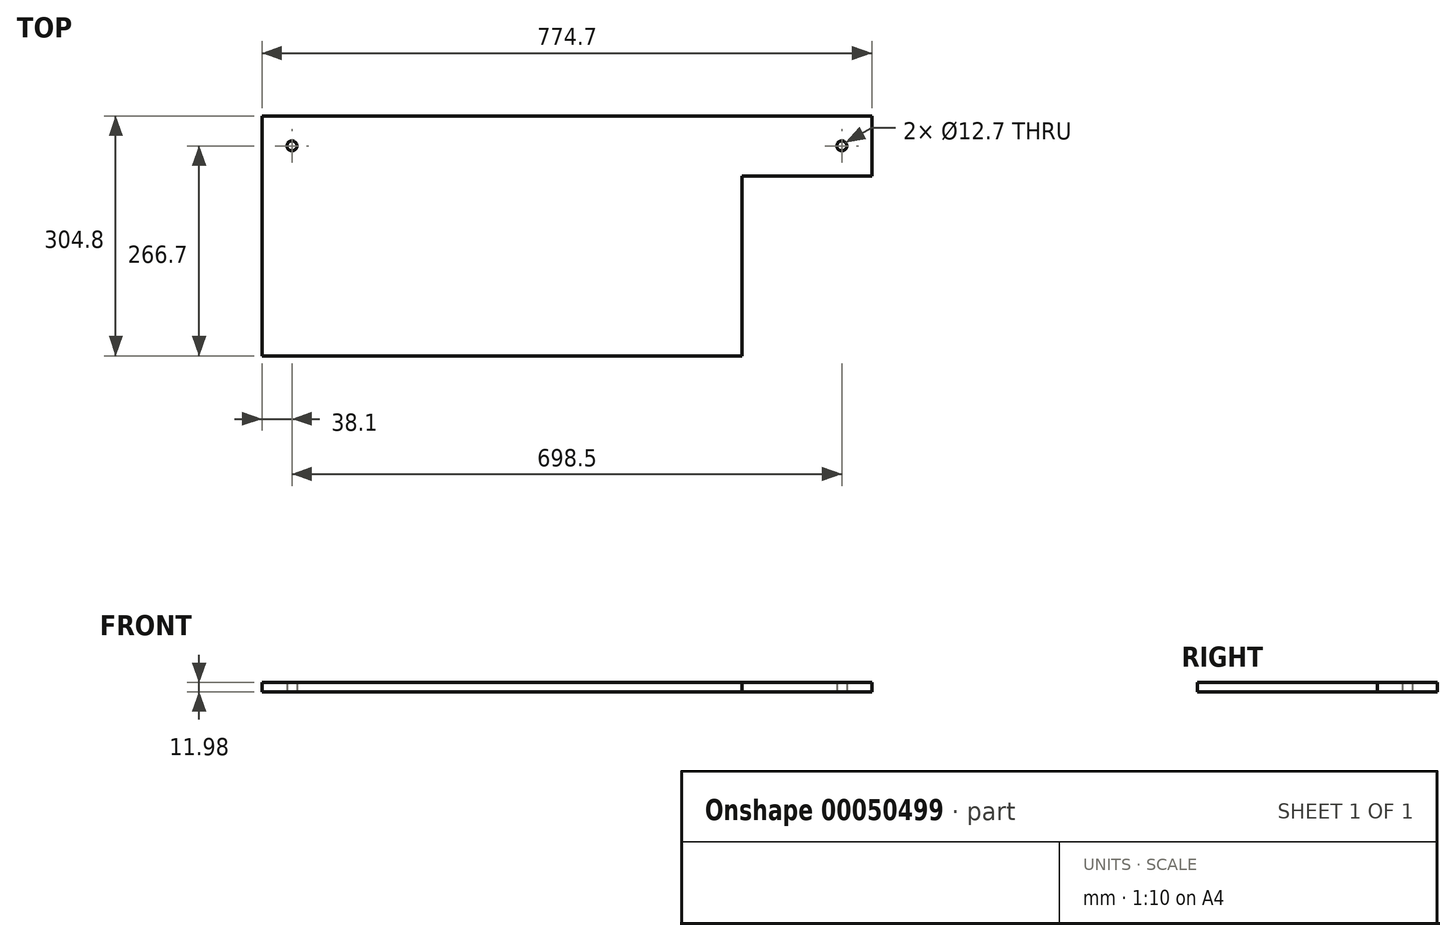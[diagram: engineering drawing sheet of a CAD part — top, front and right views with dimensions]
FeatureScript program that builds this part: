
annotation { "Feature Type Name" : "Feature", "Feature Type Description" : "" }
export const myFeature = defineFeature(function(context is Context, id is Id, definition is map)
    precondition{}
    {
        {
            var Q0;
            Q0=qCreatedBy(makeId("Top.planeOp"),FACE);
            var sketch = newSketch(context, id + "F0", { "sketchPlane" : qUnion([Q0])});
            skLineSegment(sketch, "E0.rect.bottom", {"start": v(387.35, 38.1) * mm, "end": v(-387.35, 38.1) * mm});
            skLineSegment(sketch, "E0.rect.top", {"start": v(387.35, -38.1) * mm, "end": v(222.25, -38.1) * mm});
            skLineSegment(sketch, "E0.rect.left", {"start": v(387.35, 38.1) * mm, "end": v(387.35, -38.1) * mm});
            skLineSegment(sketch, "E0.rect.right", {"start": v(-387.35, 38.1) * mm, "end": v(-387.35, -38.1) * mm});
            skPoint(sketch, "E0.rect.middle", {"position": v(0, 0) * mm});
            skLineSegment(sketch, "E1", {"start": v(222.25, -38.1) * mm, "end": v(222.25, -266.7) * mm});
            skLineSegment(sketch, "E2", {"start": v(222.25, -266.7) * mm, "end": v(-387.35, -266.7) * mm});
            skLineSegment(sketch, "E3", {"start": v(-387.35, -266.7) * mm, "end": v(-387.35, -38.1) * mm});
            skSolve(sketch);
        }
        {
            var Q0;
            Q0=qSketchRegion(id+"F0",true);
            extrude(context, id + "F1", {"entities" : qUnion([Q0]), "endBound" : BoundingType.SYMMETRIC, "depth" : 12 * mm});
        }
        {
            var Q0;
            Q0=makeQuery(id+"F1.opExtrude","CAP_FACE",FACE,{"disambiguationData":[OSD([sQuery(id+"F0.wireOp",EDGE,"E0.rect.bottom"),sQuery(id+"F0.wireOp",EDGE,"E0.rect.top"),sQuery(id+"F0.wireOp",EDGE,"E0.rect.left"),sQuery(id+"F0.wireOp",EDGE,"E0.rect.right"),sQuery(id+"F0.wireOp",EDGE,"E1"),sQuery(id+"F0.wireOp",EDGE,"E2"),sQuery(id+"F0.wireOp",EDGE,"E3")])],"isStart":true});
            var sketch = newSketch(context, id + "F2", { "sketchPlane" : qUnion([Q0])});
            skCircle(sketch, "E4", {"center": v(-349.25, 0) * mm, "radius": 6.35 * mm});
            skCircle(sketch, "E5", {"center": v(349.25, 0) * mm, "radius": 6.35 * mm});
            skSolve(sketch);
        }
        {
            var Q0;
            Q0 = qSketchRegion(id + "F2", true);
            extrude(context, id + "F3", {"entities" : qUnion([Q0]), "operationType" : NewBodyOperationType.REMOVE, "endBound" : BoundingType.UP_TO_NEXT, "oppositeDirection" : true, "depth" : 25.4 * mm});
        }
    });
